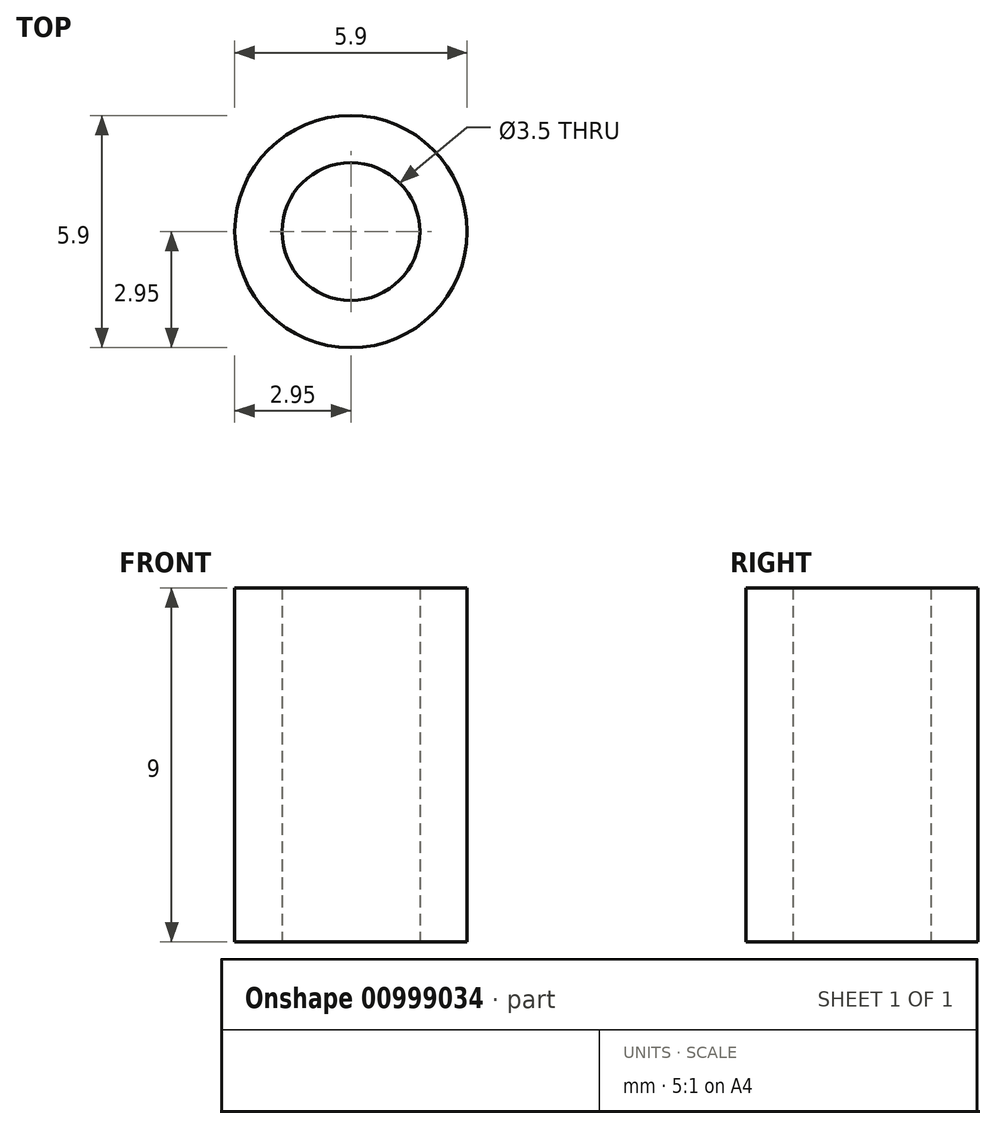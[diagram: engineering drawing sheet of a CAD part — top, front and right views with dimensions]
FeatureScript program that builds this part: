
annotation { "Feature Type Name" : "Feature", "Feature Type Description" : "" }
export const myFeature = defineFeature(function(context is Context, id is Id, definition is map)
    precondition{}
    {
        {
            var Q0;
            Q0=qCreatedBy(makeId("Top.planeOp"),FACE);
            var sketch = newSketch(context, id + "F0", { "sketchPlane" : qUnion([Q0])});
            skCircle(sketch, "E0", {"center": v(0, 0) * mm, "radius": 2.95 * mm});
            skCircle(sketch, "E1", {"center": v(0, 0) * mm, "radius": 1.75 * mm});
            skSolve(sketch);
        }
        {
            var Q0;
            Q0 = qSketchRegion(id + "F0", true);
            extrude(context, id + "F1", {"entities" : qUnion([Q0]), "depth" : 9 * mm, "offsetDistance" : 25 * mm});
        }
    });
